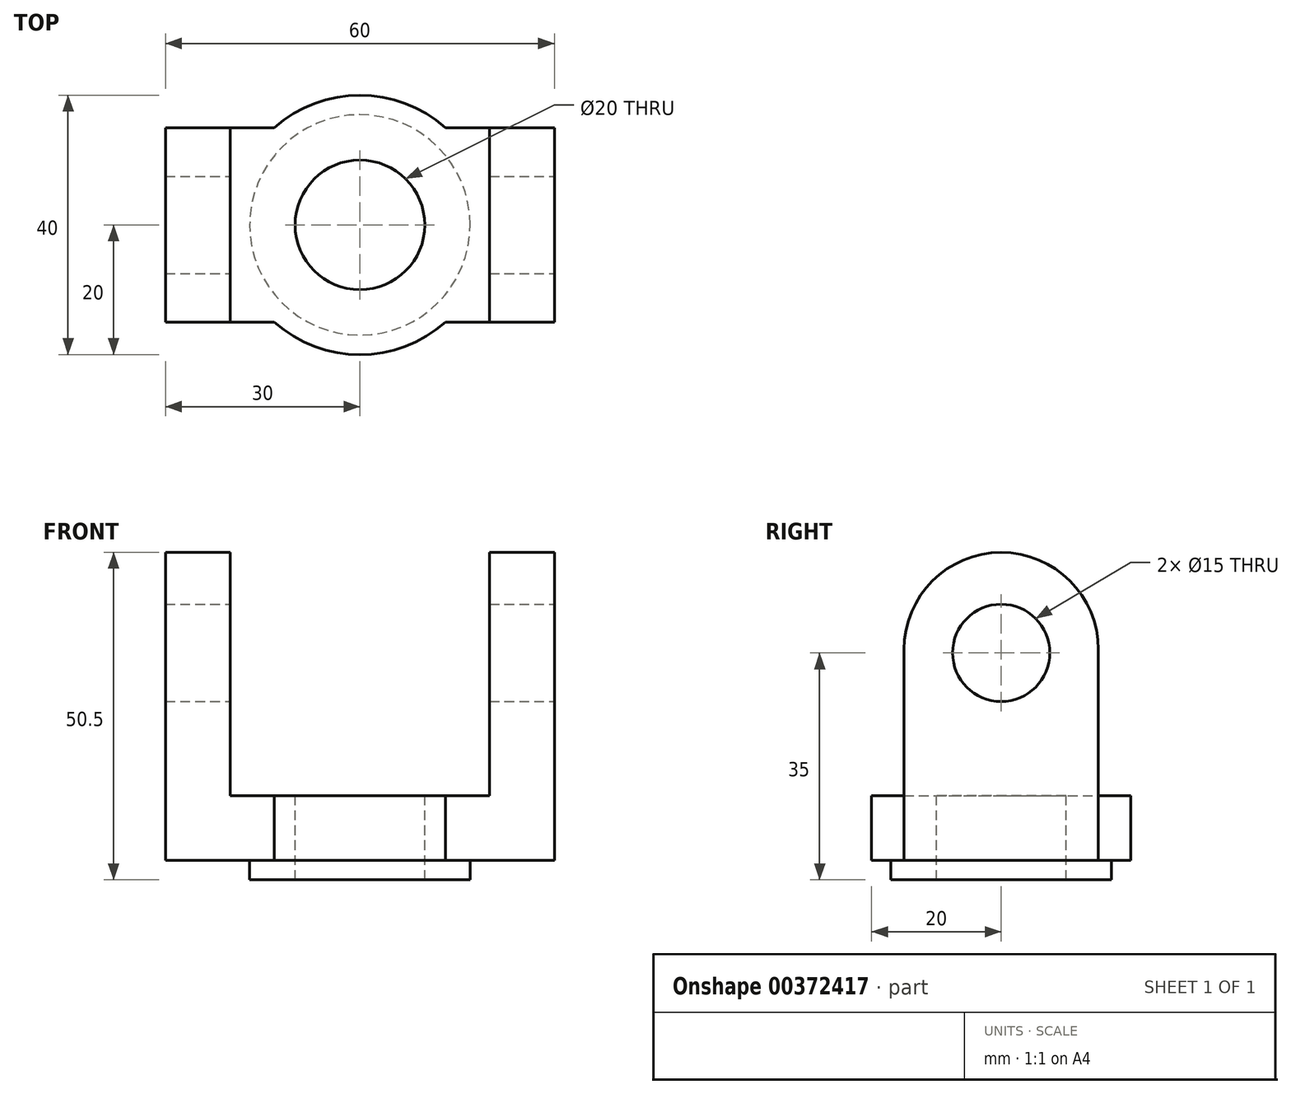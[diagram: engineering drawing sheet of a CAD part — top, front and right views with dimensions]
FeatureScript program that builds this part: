
annotation { "Feature Type Name" : "Feature", "Feature Type Description" : "" }
export const myFeature = defineFeature(function(context is Context, id is Id, definition is map)
    precondition{}
    {
        {
            var Q0;
            Q0=qCreatedBy(makeId("Top.planeOp"),FACE);
            var sketch = newSketch(context, id + "F0", { "sketchPlane" : qUnion([Q0])});
            skCircle(sketch, "E0", {"center": v(0, 0) * mm, "radius": 20 * mm});
            skSolve(sketch);
        }
        {
            var Q0;
            Q0 = qSketchRegion(id + "F0", true);
            extrude(context, id + "F1", {"entities" : qUnion([Q0]), "depth" : 10 * mm});
        }
        {
            var Q0;
            Q0=qCreatedBy(makeId("Right.planeOp"),FACE);
            var sketch = newSketch(context, id + "F2", { "sketchPlane" : qUnion([Q0])});
            skLineSegment(sketch, "E1", {"start": v(-15, 0) * mm, "end": v(15, 0) * mm});
            skLineSegment(sketch, "E2", {"start": v(15, 0) * mm, "end": v(15, 32.5) * mm});
            skLineSegment(sketch, "E3", {"start": v(-15, 0) * mm, "end": v(-15, 32.5) * mm});
            skArc(sketch, "E4", {"start": v(-15, 32.5) * mm, "mid": v(0, 47.5) * mm, "end": v(15, 32.5) * mm});
            skSolve(sketch);
        }
        {
            var Q0;
            Q0 = qSketchRegion(id + "F2", true);
            extrude(context, id + "F3", {"entities" : qUnion([Q0]), "operationType" : NewBodyOperationType.ADD, "endBound" : BoundingType.SYMMETRIC, "depth" : 60 * mm});
        }
        {
            var Q0;
            Q0=qCreatedBy(makeId("Right.planeOp"),FACE);
            var sketch = newSketch(context, id + "F4", { "sketchPlane" : qUnion([Q0])});
            skLineSegment(sketch, "E5.bottom", {"start": v(-15, 47.5) * mm, "end": v(15, 47.5) * mm});
            skLineSegment(sketch, "E5.top", {"start": v(-15, 10) * mm, "end": v(15, 10) * mm});
            skLineSegment(sketch, "E5.left", {"start": v(-15, 47.5) * mm, "end": v(-15, 10) * mm});
            skLineSegment(sketch, "E5.right", {"start": v(15, 47.5) * mm, "end": v(15, 10) * mm});
            skSolve(sketch);
        }
        {
            var Q0;
            Q0 = qSketchRegion(id + "F4", true);
            extrude(context, id + "F5", {"entities" : qUnion([Q0]), "operationType" : NewBodyOperationType.REMOVE, "endBound" : BoundingType.SYMMETRIC, "oppositeDirection" : true, "depth" : 40 * mm});
        }
        {
            var Q0;
            Q0=qCreatedBy(makeId("Right.planeOp"),FACE);
            var sketch = newSketch(context, id + "F6", { "sketchPlane" : qUnion([Q0])});
            skCircle(sketch, "E6", {"center": v(0, 32) * mm, "radius": 7.5 * mm});
            skSolve(sketch);
        }
        {
            var Q0;
            Q0 = qSketchRegion(id + "F6", true);
            extrude(context, id + "F7", {"entities" : qUnion([Q0]), "operationType" : NewBodyOperationType.REMOVE, "endBound" : BoundingType.THROUGH_ALL, "oppositeDirection" : true, "depth" : 25 * mm, "hasSecondDirection" : true, "secondDirectionBound" : SecondDirectionBoundingType.THROUGH_ALL, "secondDirectionOppositeDirection" : false, "secondDirectionDepth" : 25 * mm});
        }
        {
            var Q0;
            Q0=makeQuery(id+"F3.boolean.opBoolean","MERGE",FACE,{"derivedFrom":[makeQuery(id+"F1.opExtrude","CAP_FACE",FACE,{"disambiguationData":[OSD([sQuery(id+"F0.wireOp",EDGE,"E0")])],"isStart":true}),makeQuery(id+"F3.opExtrude","SWEPT_FACE",FACE,{"disambiguationData":[OSD([sQuery(id+"F2.wireOp",EDGE,"E1")])]})]});
            var sketch = newSketch(context, id + "F8", { "sketchPlane" : qUnion([Q0])});
            skCircle(sketch, "E7", {"center": v(0, 0) * mm, "radius": 17 * mm});
            skSolve(sketch);
        }
        {
            var Q0;
            Q0 = qSketchRegion(id + "F8", true);
            extrude(context, id + "F9", {"entities" : qUnion([Q0]), "operationType" : NewBodyOperationType.ADD, "depth" : 3 * mm});
        }
        {
            var Q0;
            {var subQ0=sQuery(id+"F0.wireOp",EDGE,"E0");var subQ2=makeQuery(id+"F1.opExtrude","CAP_FACE",FACE,{"disambiguationData":[OSD([subQ0])],"isStart":false});Q0=makeQuery(id+"F5.boolean.opBoolean","MERGE",FACE,{"derivedFrom":[makeQuery(id+"F3.boolean.opBoolean","SPLIT",FACE,{"disambiguationData":[TD([makeQuery(id+"F3.opExtrude","SWEPT_FACE",FACE,{"disambiguationData":[OSD([sQuery(id+"F2.wireOp",EDGE,"E2")])]})])],"derivedFrom":subQ2}),makeQuery(id+"F3.boolean.opBoolean","SPLIT",FACE,{"disambiguationData":[TD([makeQuery(id+"F3.opExtrude","SWEPT_FACE",FACE,{"disambiguationData":[OSD([sQuery(id+"F2.wireOp",EDGE,"E3")])]})])],"derivedFrom":subQ2}),makeQuery(id+"F5.opExtrude","SWEPT_FACE",FACE,{"disambiguationData":[OSD([sQuery(id+"F4.wireOp",EDGE,"E5.top")])]})]});}
            var sketch = newSketch(context, id + "F10", { "sketchPlane" : qUnion([Q0])});
            skCircle(sketch, "E8", {"center": v(0, 0) * mm, "radius": 10 * mm});
            skSolve(sketch);
        }
        {
            var Q0;
            Q0 = qSketchRegion(id + "F10", true);
            extrude(context, id + "F11", {"entities" : qUnion([Q0]), "operationType" : NewBodyOperationType.REMOVE, "endBound" : BoundingType.THROUGH_ALL, "oppositeDirection" : true, "depth" : 25 * mm});
        }
    });
